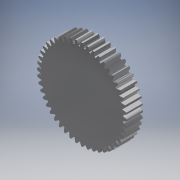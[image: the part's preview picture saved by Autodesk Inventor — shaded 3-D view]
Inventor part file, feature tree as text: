
AUTODESK INVENTOR PART (.ipt)
format: ipt  version: 2019 (Build 230136000, 136)  size: 327,680 bytes
history: native  units: mm (DEFAULTED — no unit token found)
features: plane x3, other x3, sketch x2, extrude x1
ambient origin geometry x8: Origin, YZ Plane, XZ Plane, XY Plane, X Axis, Y Axis, Z Axis, Center Point
bodies: Solid1 (feature_tree)
feature tree (9):
  extrude  "Extrusion1"  Depth=1.8mm TaperAngle=0.0deg
  plane  "Work Plane2"
  plane  "Work Plane8"
  plane  "Work Plane9"
  other  "Spur Gear"
  sketch  "Sketch1"  dims[d0=9.95mm d1=1.8mm d2=0.0mm]
  sketch  "Sketch2"  dims[d3=9.56mm d4=10.0mm d5=0.0mm d16=5.975mm d17=0.0mm d34=0.654498mm d39=0.0mm d41=0.0mm d43=5.975mm d46=5.975mm d47=0.0mm d48=0.0mm]
  other  "Srf1"
  other  "Pitch Diameter"
